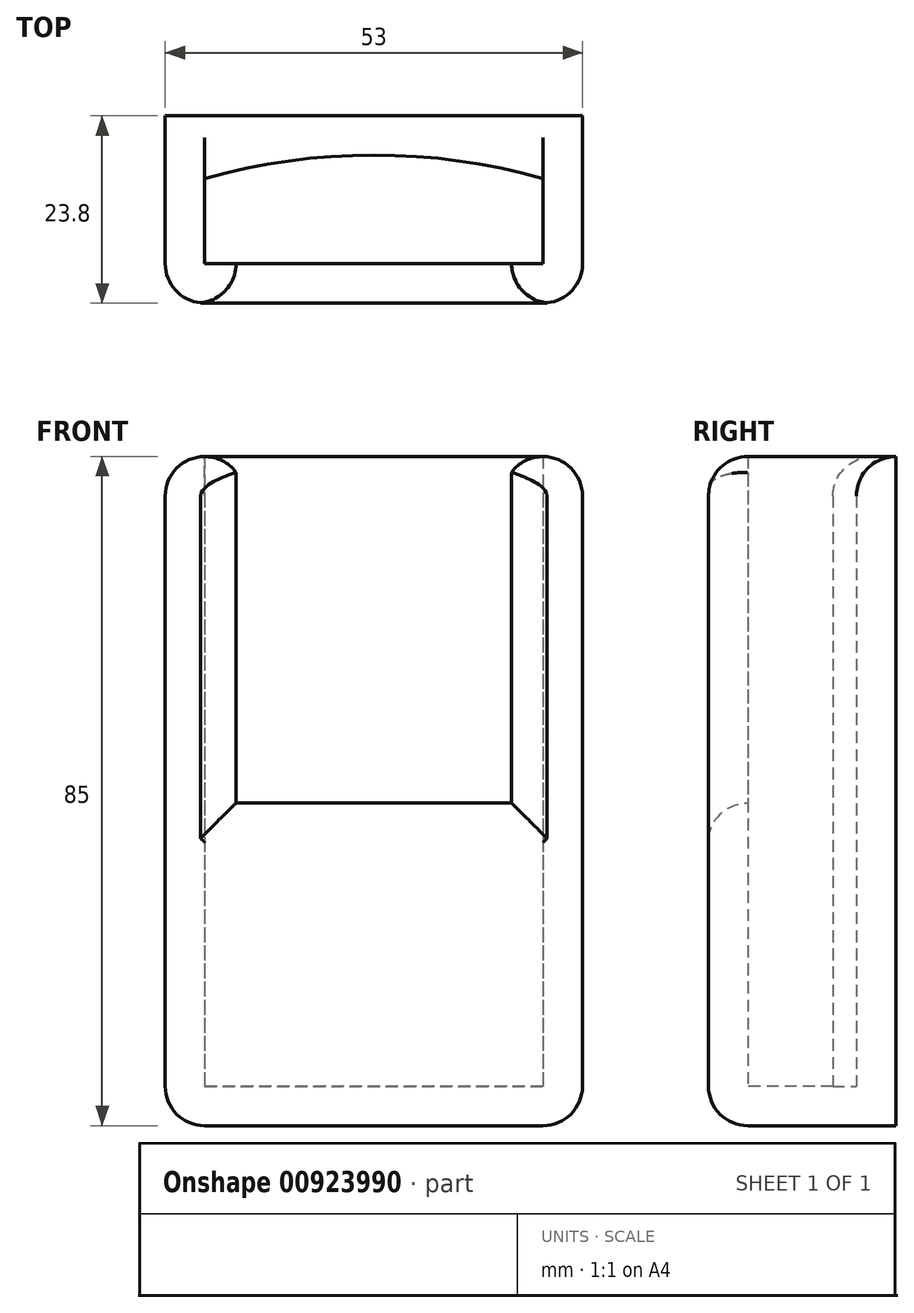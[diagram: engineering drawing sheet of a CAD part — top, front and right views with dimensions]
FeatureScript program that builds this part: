
annotation { "Feature Type Name" : "Feature", "Feature Type Description" : "" }
export const myFeature = defineFeature(function(context is Context, id is Id, definition is map)
    precondition{}
    {
        {
            var Q0;
            Q0=qCreatedBy(makeId("Top.planeOp"),FACE);
            var sketch = newSketch(context, id + "F0", { "sketchPlane" : qUnion([Q0])});
            skLineSegment(sketch, "E0.bottom", {"start": v(-23.75, 6.9) * mm, "end": v(19.25, 6.9) * mm});
            skLineSegment(sketch, "E0.top", {"start": v(-23.75, -6.9) * mm, "end": v(19.25, -6.9) * mm});
            skLineSegment(sketch, "E0.left", {"start": v(-23.75, 6.9) * mm, "end": v(-23.75, -6.9) * mm});
            skLineSegment(sketch, "E0.right", {"start": v(19.25, 6.9) * mm, "end": v(19.25, -6.9) * mm});
            skLineSegment(sketch, "E1.bottom", {"start": v(-28.75, 11.9) * mm, "end": v(24.25, 11.9) * mm});
            skLineSegment(sketch, "E1.top", {"start": v(-28.75, -11.9) * mm, "end": v(24.25, -11.9) * mm});
            skLineSegment(sketch, "E1.left", {"start": v(-28.75, 11.9) * mm, "end": v(-28.75, -11.9) * mm});
            skLineSegment(sketch, "E1.right", {"start": v(24.25, 11.9) * mm, "end": v(24.25, -11.9) * mm});
            skSolve(sketch);
        }
        {
            var Q0;
            Q0=qSketchRegion(id+"F0",true);
            extrude(context, id + "F1", {"entities" : qUnion([Q0]), "depth" : 80 * mm, "offsetDistance" : 25 * mm});
        }
        {
            var Q0;
            Q0=makeQuery(id+"F0.imprint","IMPRINT",FACE,{"disambiguationData":[TD([[makeQuery(id+"F0.imprint","IMPRINT",EDGE,{"derivedFrom":sQuery(id+"F0.wireOp",EDGE,"E0.bottom")}),1.0]])]});
            var Q1;
            Q1=makeQuery(id+"F0.imprint","IMPRINT",FACE,{"disambiguationData":[TD([[makeQuery(id+"F0.imprint","IMPRINT",EDGE,{"derivedFrom":sQuery(id+"F0.wireOp",EDGE,"E0.bottom")}),-1.0]])]});
            extrude(context, id + "F2", {"entities" : qUnion([Q0, Q1]), "operationType" : NewBodyOperationType.ADD, "oppositeDirection" : true, "depth" : 5 * mm, "offsetDistance" : 25 * mm});
        }
        {
            var Q0;
            Q0=makeQuery(id+"F1.opExtrude","SWEPT_FACE",FACE,{"disambiguationData":[OSD([sQuery(id+"F0.wireOp",EDGE,"E0.top")])]});
            var sketch = newSketch(context, id + "F3", { "sketchPlane" : qUnion([Q0])});
            skLineSegment(sketch, "E2.bottom", {"start": v(19.75, 80) * mm, "end": v(-15.25, 80) * mm});
            skLineSegment(sketch, "E2.top", {"start": v(19.75, 36) * mm, "end": v(-15.25, 36) * mm});
            skLineSegment(sketch, "E2.left", {"start": v(19.75, 80) * mm, "end": v(19.75, 36) * mm});
            skLineSegment(sketch, "E2.right", {"start": v(-15.25, 80) * mm, "end": v(-15.25, 36) * mm});
            skSolve(sketch);
        }
        {
            var Q0;
            Q0=qSketchRegion(id+"F3",true);
            extrude(context, id + "F4", {"entities" : qUnion([Q0]), "operationType" : NewBodyOperationType.REMOVE, "oppositeDirection" : true, "depth" : 25 * mm, "offsetDistance" : 25 * mm});
        }
        {
            var Q0;
            Q0=makeQuery(id+"F2.opExtrude","CAP_EDGE",EDGE,{"disambiguationData":[OSD([sQuery(id+"F0.wireOp",EDGE,"E1.top")])],"isStart":false});
            var Q1;
            {var subQ0=sQuery(id+"F0.wireOp",EDGE,"E1.left");var subQ1=sQuery(id+"F0.wireOp",EDGE,"E1.top");Q1=makeQuery(id+"F2.boolean.opBoolean","MERGE",EDGE,{"derivedFrom":[makeQuery(id+"F1.opExtrude","SWEPT_EDGE",EDGE,{"disambiguationData":[OSD([subQ1,subQ0])]}),makeQuery(id+"F2.opExtrude","SWEPT_EDGE",EDGE,{"disambiguationData":[OSD([subQ1,subQ0])]})]});}
            var Q2;
            {var subQ0=sQuery(id+"F0.wireOp",EDGE,"E1.right");var subQ1=sQuery(id+"F0.wireOp",EDGE,"E1.top");Q2=makeQuery(id+"F2.boolean.opBoolean","MERGE",EDGE,{"derivedFrom":[makeQuery(id+"F1.opExtrude","SWEPT_EDGE",EDGE,{"disambiguationData":[OSD([subQ1,subQ0])]}),makeQuery(id+"F2.opExtrude","SWEPT_EDGE",EDGE,{"disambiguationData":[OSD([subQ1,subQ0])]})]});}
            var Q3;
            {var subQ0=sQuery(id+"F0.wireOp",EDGE,"E1.top");Q3=makeQuery(id+"F4.boolean.opBoolean","INTERSECT",EDGE,{"derivedFrom":[makeQuery(id+"F2.boolean.opBoolean","MERGE",FACE,{"derivedFrom":[makeQuery(id+"F1.opExtrude","SWEPT_FACE",FACE,{"disambiguationData":[OSD([subQ0])]}),makeQuery(id+"F2.opExtrude","SWEPT_FACE",FACE,{"disambiguationData":[OSD([subQ0])]})]}),makeQuery(id+"F4.opExtrude","SWEPT_FACE",FACE,{"disambiguationData":[OSD([sQuery(id+"F3.wireOp",EDGE,"E2.top")])]})]});}
            var Q4;
            {var subQ0=sQuery(id+"F0.wireOp",EDGE,"E1.top");Q4=makeQuery(id+"F4.boolean.opBoolean","INTERSECT",EDGE,{"derivedFrom":[makeQuery(id+"F2.boolean.opBoolean","MERGE",FACE,{"derivedFrom":[makeQuery(id+"F1.opExtrude","SWEPT_FACE",FACE,{"disambiguationData":[OSD([subQ0])]}),makeQuery(id+"F2.opExtrude","SWEPT_FACE",FACE,{"disambiguationData":[OSD([subQ0])]})]}),makeQuery(id+"F4.opExtrude","SWEPT_FACE",FACE,{"disambiguationData":[OSD([sQuery(id+"F3.wireOp",EDGE,"E2.left")])]})]});}
            var Q5;
            {var subQ0=sQuery(id+"F0.wireOp",EDGE,"E1.top");Q5=makeQuery(id+"F4.boolean.opBoolean","INTERSECT",EDGE,{"derivedFrom":[makeQuery(id+"F2.boolean.opBoolean","MERGE",FACE,{"derivedFrom":[makeQuery(id+"F1.opExtrude","SWEPT_FACE",FACE,{"disambiguationData":[OSD([subQ0])]}),makeQuery(id+"F2.opExtrude","SWEPT_FACE",FACE,{"disambiguationData":[OSD([subQ0])]})]}),makeQuery(id+"F4.opExtrude","SWEPT_FACE",FACE,{"disambiguationData":[OSD([sQuery(id+"F3.wireOp",EDGE,"E2.right")])]})]});}
            fillet(context, id + "F5", {"entities" : qUnion([Q0, Q1, Q2, Q3, Q4, Q5]), "radius" : 5 * mm, "tangentPropagation" : true, "allowEdgeOverflow" : false});
        }
        {
            var Q0;
            Q0=makeQuery(id+"F2.opExtrude","CAP_EDGE",EDGE,{"disambiguationData":[OSD([sQuery(id+"F0.wireOp",EDGE,"E1.right")])],"isStart":false});
            var Q1;
            Q1=makeQuery(id+"F2.opExtrude","CAP_EDGE",EDGE,{"disambiguationData":[OSD([sQuery(id+"F0.wireOp",EDGE,"E1.left")])],"isStart":false});
            fillet(context, id + "F6", {"entities" : qUnion([Q0, Q1]), "radius" : 5 * mm, "tangentPropagation" : true, "allowEdgeOverflow" : false});
        }
        {
            var Q0;
            {var subQ0=sQuery(id+"F0.wireOp",EDGE,"E1.right");var subQ1=sQuery(id+"F0.wireOp",EDGE,"E1.top");Q0=makeQuery(id+"F5.opFillet","BLEND_EDGE",EDGE,{"blendedFrom":[makeQuery(id+"F2.boolean.opBoolean","MERGE",EDGE,{"derivedFrom":[makeQuery(id+"F1.opExtrude","SWEPT_EDGE",EDGE,{"disambiguationData":[OSD([subQ1,subQ0])]}),makeQuery(id+"F2.opExtrude","SWEPT_EDGE",EDGE,{"disambiguationData":[OSD([subQ1,subQ0])]})]}),makeQuery(id+"F1.opExtrude","CAP_FACE",FACE,{"disambiguationData":[OSD([sQuery(id+"F0.wireOp",EDGE,"E0.bottom"),sQuery(id+"F0.wireOp",EDGE,"E0.top"),sQuery(id+"F0.wireOp",EDGE,"E0.left"),sQuery(id+"F0.wireOp",EDGE,"E0.right"),sQuery(id+"F0.wireOp",EDGE,"E1.bottom"),subQ1,sQuery(id+"F0.wireOp",EDGE,"E1.left"),subQ0])],"isStart":false})],"blendedInto":[makeQuery(id+"F1.opExtrude","CAP_FACE",FACE,{"disambiguationData":[OSD([sQuery(id+"F0.wireOp",EDGE,"E0.bottom"),sQuery(id+"F0.wireOp",EDGE,"E0.top"),sQuery(id+"F0.wireOp",EDGE,"E0.left"),sQuery(id+"F0.wireOp",EDGE,"E0.right"),sQuery(id+"F0.wireOp",EDGE,"E1.bottom"),subQ1,sQuery(id+"F0.wireOp",EDGE,"E1.left"),subQ0])],"isStart":false})]});}
            var Q1;
            Q1=makeQuery(id+"F1.opExtrude","CAP_EDGE",EDGE,{"disambiguationData":[OSD([sQuery(id+"F0.wireOp",EDGE,"E1.left")])],"isStart":false});
            fillet(context, id + "F7", {"entities" : qUnion([Q0, Q1]), "radius" : 5 * mm, "tangentPropagation" : true, "allowEdgeOverflow" : false});
        }
        {
            var Q0;
            Q0=makeQuery(id+"F2.opExtrude","CAP_FACE",FACE,{"disambiguationData":[OSD([sQuery(id+"F0.wireOp",EDGE,"E1.bottom"),sQuery(id+"F0.wireOp",EDGE,"E1.top"),sQuery(id+"F0.wireOp",EDGE,"E1.left"),sQuery(id+"F0.wireOp",EDGE,"E1.right")])],"isStart":true});
            var sketch = newSketch(context, id + "F8", { "sketchPlane" : qUnion([Q0])});
            skLineSegment(sketch, "E3", {"start": v(-2.25, 18.88) * mm, "end": v(-2.25, -17.9) * mm, "construction": true});
            skLineSegment(sketch, "E4", {"start": v(29.93, 3.9) * mm, "end": v(-32.65, 3.9) * mm, "construction": true});
            skArc(sketch, "E5", {"start": v(19.25, 3.9) * mm, "mid": v(-2.25, 6.9) * mm, "end": v(-23.75, 3.9) * mm});
            skPoint(sketch, "E5.first.point", {"position": v(-23.75, 3.9) * mm});
            skPoint(sketch, "E5.second.point", {"position": v(-2.25, 6.9) * mm});
            skPoint(sketch, "E5.third.point", {"position": v(19.25, 3.9) * mm});
            skLineSegment(sketch, "E6", {"start": v(19.25, 3.9) * mm, "end": v(19.25, 6.9) * mm});
            skLineSegment(sketch, "E7", {"start": v(19.25, 6.9) * mm, "end": v(-23.75, 6.9) * mm});
            skLineSegment(sketch, "E8", {"start": v(-23.75, 6.9) * mm, "end": v(-23.75, 3.9) * mm});
            skSolve(sketch);
        }
        {
            var Q0;
            {var subQ0=sQuery(id+"F8.wireOp",EDGE,"E6");Q0=makeQuery(id+"F8.imprint","IMPRINT",FACE,{"disambiguationData":[TD([[makeQuery(id+"F8.imprint","IMPRINT",EDGE,{"derivedFrom":subQ0}),-1.0]])]});}
            var Q1;
            {var subQ0=sQuery(id+"F8.wireOp",EDGE,"E8");Q1=makeQuery(id+"F8.imprint","IMPRINT",FACE,{"disambiguationData":[TD([[makeQuery(id+"F8.imprint","IMPRINT",EDGE,{"derivedFrom":subQ0}),1.0]])]});}
            extrude(context, id + "F9", {"entities" : qUnion([Q0, Q1]), "operationType" : NewBodyOperationType.ADD, "depth" : 80 * mm, "offsetDistance" : 25 * mm});
        }
        {
            var Q0;
            {var subQ0=sQuery(id+"F8.wireOp",EDGE,"E5");var subQ1=makeQuery(id+"F8.imprint","INTERSECT",VERTEX,{"derivedFrom":[subQ0,sQuery(id+"F8.wireOp",EDGE,"E7")]});Q0=makeQuery(id+"F9.boolean.opBoolean","MERGE",EDGE,{"derivedFrom":[makeQuery(id+"F9.opExtrude","CAP_EDGE",EDGE,{"disambiguationData":[OSD([subQ0]),TDD([makeQuery(id+"F8.imprint","IMPRINT",EDGE,{"disambiguationData":[TD([[subQ1,1.0]])],"derivedFrom":subQ0})])],"isStart":false}),makeQuery(id+"F9.opExtrude","CAP_EDGE",EDGE,{"disambiguationData":[OSD([subQ0]),TDD([makeQuery(id+"F8.imprint","IMPRINT",EDGE,{"disambiguationData":[TD([[subQ1,-1.0]])],"derivedFrom":subQ0})])],"isStart":false})]});}
            fillet(context, id + "F10", {"entities" : qUnion([Q0]), "radius" : 5 * mm, "tangentPropagation" : true, "allowEdgeOverflow" : false});
        }
    });
